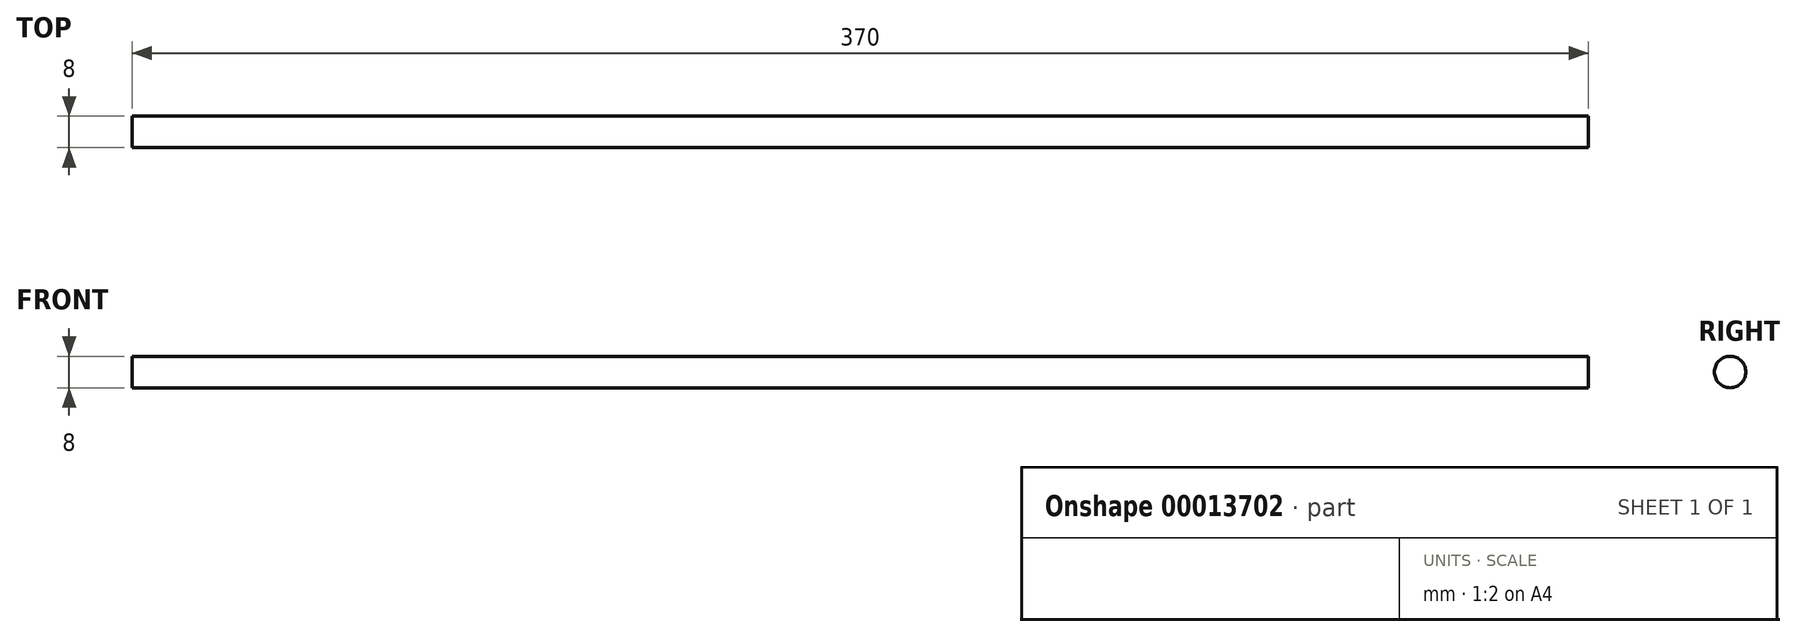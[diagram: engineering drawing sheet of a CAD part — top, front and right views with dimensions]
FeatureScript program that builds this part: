
annotation { "Feature Type Name" : "Feature", "Feature Type Description" : "" }
export const myFeature = defineFeature(function(context is Context, id is Id, definition is map)
    precondition{}
    {
        {
            var Q0;
            Q0=qCreatedBy(makeId("Right.planeOp"),FACE);
            var sketch = newSketch(context, id + "F0", { "sketchPlane" : qUnion([Q0])});
            skCircle(sketch, "E0", {"center": v(0, 0) * mm, "radius": 4 * mm});
            skSolve(sketch);
        }
        {
            var Q0;
            Q0=makeQuery(id+"F0.imprint","IMPRINT",FACE,{"disambiguationData":[TD([[makeQuery(id+"F0.imprint","IMPRINT",EDGE,{"derivedFrom":sQuery(id+"F0.wireOp",EDGE,"E0")}),1.0]])]});
            extrude(context, id + "F1", {"entities" : qUnion([Q0]), "depth" : 370 * mm});
        }
    });
